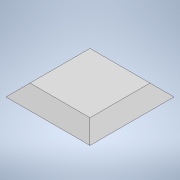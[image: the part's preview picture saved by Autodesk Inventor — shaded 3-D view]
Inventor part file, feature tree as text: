
AUTODESK INVENTOR PART (.ipt)
format: ipt  version: 2021 (Build 250183000, 183)  size: 93,696 bytes
history: native  units: in
note: dims shown in document units (in); Inventor stores cm internally (conversion verified against a paired STEP export)
features: extrude x1, chamfer x1, sketch x1
ambient origin geometry x8: Origin, YZ Plane, XZ Plane, XY Plane, X Axis, Y Axis, Z Axis, Center Point
bodies: Solid1 (feature_tree)
feature tree (3):
  extrude  "Extrusion1"  Depth=0.0787in
  chamfer  "Chamfer1"  Distance=0.0787in
  sketch  "Sketch1"  dims[d0=0.5512in d1=0.5512in d2=0.0787in d3=0.0in d4=0.0787in d5=0.0787in d6=45.0deg]
